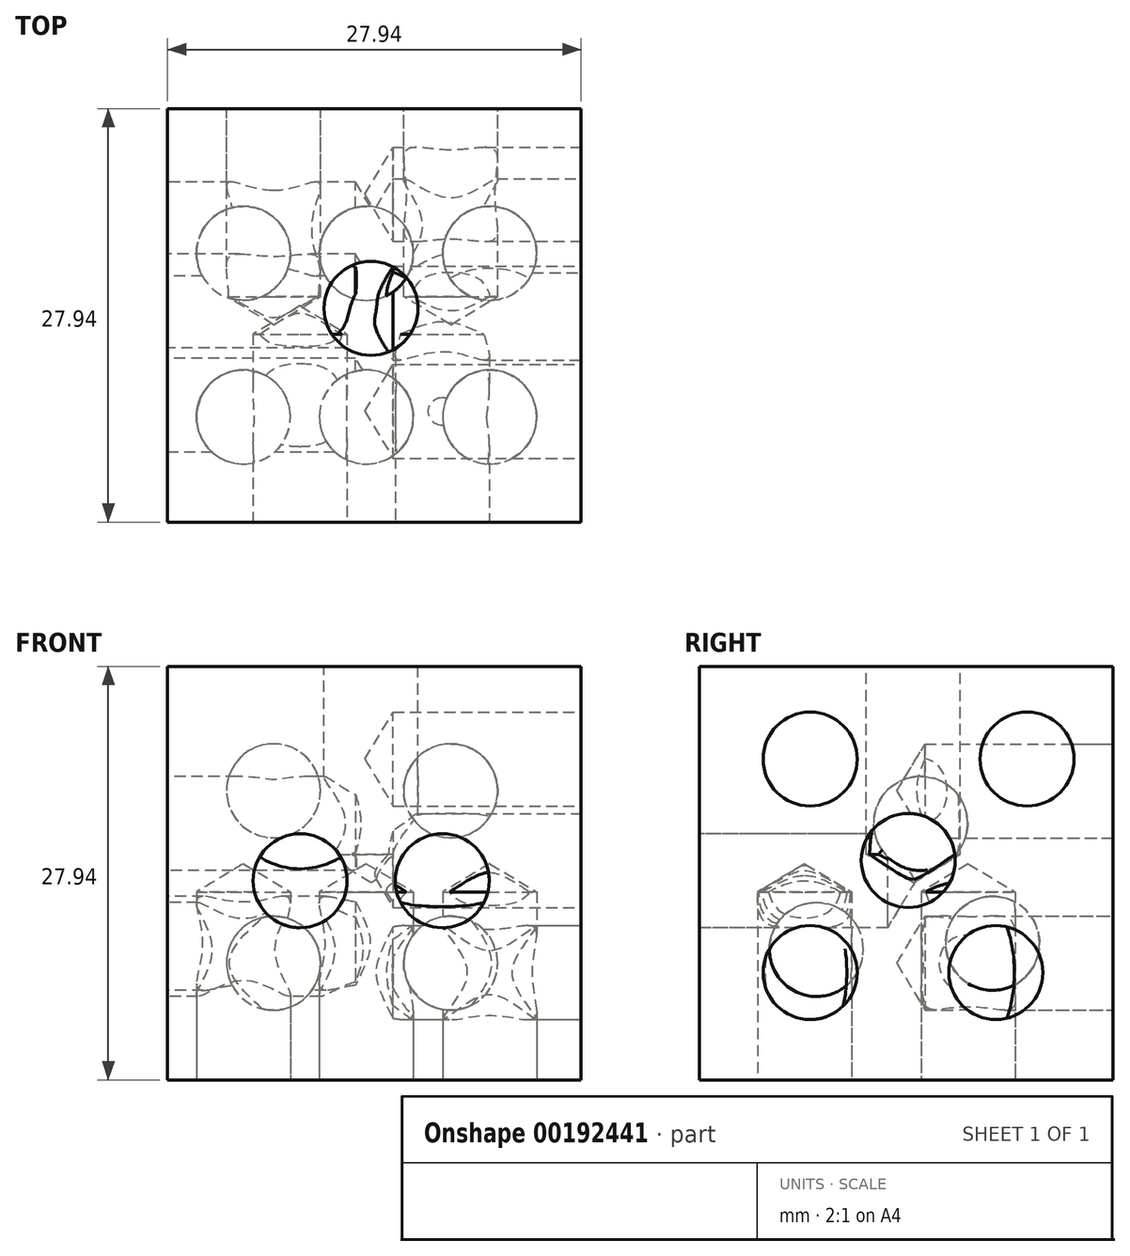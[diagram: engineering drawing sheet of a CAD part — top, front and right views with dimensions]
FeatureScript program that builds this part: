
annotation { "Feature Type Name" : "Feature", "Feature Type Description" : "" }
export const myFeature = defineFeature(function(context is Context, id is Id, definition is map)
    precondition{}
    {
        {
            var Q0;
            Q0=qCreatedBy(makeId("Top.planeOp"),FACE);
            var sketch = newSketch(context, id + "F0", { "sketchPlane" : qUnion([Q0])});
            skLineSegment(sketch, "E0.bottom", {"start": v(0, 0) * mm, "end": v(27.94, 0) * mm});
            skLineSegment(sketch, "E0.top", {"start": v(0, 27.94) * mm, "end": v(27.94, 27.94) * mm});
            skLineSegment(sketch, "E0.left", {"start": v(0, 0) * mm, "end": v(0, 27.94) * mm});
            skLineSegment(sketch, "E0.right", {"start": v(27.94, 0) * mm, "end": v(27.94, 27.94) * mm});
            skSolve(sketch);
        }
        {
            var Q0;
            Q0 = qSketchRegion(id + "F0", true);
            extrude(context, id + "F1", {"entities" : qUnion([Q0]), "depth" : 27.94 * mm});
        }
        {
            var Q0;
            Q0=makeQuery(id+"F1.opExtrude","CAP_FACE",FACE,{"disambiguationData":[OSD([sQuery(id+"F0.wireOp",EDGE,"E0.bottom"),sQuery(id+"F0.wireOp",EDGE,"E0.top"),sQuery(id+"F0.wireOp",EDGE,"E0.left"),sQuery(id+"F0.wireOp",EDGE,"E0.right")])],"isStart":false});
            var sketch = newSketch(context, id + "F2", { "sketchPlane" : qUnion([Q0])});
            skPoint(sketch, "E1", {"position": v(13.75, 14.44) * mm});
            skSolve(sketch);
        }
        {
            var Q0;
            Q0=makeQuery(id+"F1.opExtrude","SWEPT_FACE",FACE,{"disambiguationData":[OSD([sQuery(id+"F0.wireOp",EDGE,"E0.bottom")])]});
            var sketch = newSketch(context, id + "F3", { "sketchPlane" : qUnion([Q0])});
            skPoint(sketch, "E2", {"position": v(8.96, 13.45) * mm});
            skPoint(sketch, "E3", {"position": v(18.56, 13.45) * mm});
            skSolve(sketch);
        }
        {
            var Q0;
            Q0=makeQuery(id+"F1.opExtrude","SWEPT_FACE",FACE,{"disambiguationData":[OSD([sQuery(id+"F0.wireOp",EDGE,"E0.left")])]});
            var sketch = newSketch(context, id + "F4", { "sketchPlane" : qUnion([Q0])});
            skPoint(sketch, "E4", {"position": v(-7.9, 8.81) * mm});
            skPoint(sketch, "E5", {"position": v(-19.8, 9.22) * mm});
            skPoint(sketch, "E6", {"position": v(-14.94, 17.33) * mm});
            skSolve(sketch);
        }
        {
            var Q0;
            Q0=makeQuery(id+"F1.opExtrude","SWEPT_FACE",FACE,{"disambiguationData":[OSD([sQuery(id+"F0.wireOp",EDGE,"E0.top")])]});
            var sketch = newSketch(context, id + "F5", { "sketchPlane" : qUnion([Q0])});
            skPoint(sketch, "E7", {"position": v(-19.13, 19.53) * mm});
            skPoint(sketch, "E8", {"position": v(-7.16, 19.53) * mm});
            skPoint(sketch, "E9", {"position": v(-7.16, 7.88) * mm});
            skPoint(sketch, "E10", {"position": v(-19.13, 7.88) * mm});
            skSolve(sketch);
        }
        {
            var Q0;
            Q0=makeQuery(id+"F1.opExtrude","SWEPT_FACE",FACE,{"disambiguationData":[OSD([sQuery(id+"F0.wireOp",EDGE,"E0.right")])]});
            var sketch = newSketch(context, id + "F6", { "sketchPlane" : qUnion([Q0])});
            skPoint(sketch, "E11", {"position": v(7.47, 7.25) * mm});
            skPoint(sketch, "E12", {"position": v(7.47, 21.67) * mm});
            skPoint(sketch, "E13", {"position": v(22.13, 21.67) * mm});
            skPoint(sketch, "E14", {"position": v(20.02, 7.25) * mm});
            skPoint(sketch, "E15", {"position": v(14.1, 14.83) * mm});
            skSolve(sketch);
        }
        {
            var Q0;
            Q0=makeQuery(id+"F1.opExtrude","CAP_FACE",FACE,{"disambiguationData":[OSD([sQuery(id+"F0.wireOp",EDGE,"E0.bottom"),sQuery(id+"F0.wireOp",EDGE,"E0.top"),sQuery(id+"F0.wireOp",EDGE,"E0.left"),sQuery(id+"F0.wireOp",EDGE,"E0.right")])],"isStart":true});
            var sketch = newSketch(context, id + "F7", { "sketchPlane" : qUnion([Q0])});
            skPoint(sketch, "E16", {"position": v(21.77, -7.1) * mm});
            skPoint(sketch, "E17", {"position": v(13.43, -7.1) * mm});
            skPoint(sketch, "E18", {"position": v(5.13, -7.1) * mm});
            skPoint(sketch, "E19", {"position": v(5.13, -18.16) * mm});
            skPoint(sketch, "E20", {"position": v(13.43, -18.16) * mm});
            skPoint(sketch, "E21", {"position": v(21.77, -18.16) * mm});
            skSolve(sketch);
        }
        {
            var Q0;
            Q0=sQuery(id+"F2.wireOp",VERTEX,"E1");
            var Q1;
            Q1=sQuery(id+"F5.wireOp",VERTEX,"E8");
            var Q2;
            Q2=sQuery(id+"F5.wireOp",VERTEX,"E7");
            var Q3;
            Q3=sQuery(id+"F6.wireOp",VERTEX,"E13");
            var Q4;
            Q4=sQuery(id+"F6.wireOp",VERTEX,"E12");
            var Q5;
            Q5=sQuery(id+"F5.wireOp",VERTEX,"E10");
            var Q6;
            Q6=sQuery(id+"F6.wireOp",VERTEX,"E15");
            var Q7;
            Q7=sQuery(id+"F6.wireOp",VERTEX,"E14");
            var Q8;
            Q8=sQuery(id+"F7.wireOp",VERTEX,"E21");
            var Q9;
            Q9=sQuery(id+"F7.wireOp",VERTEX,"E16");
            var Q10;
            Q10=sQuery(id+"F7.wireOp",VERTEX,"E17");
            var Q11;
            Q11=sQuery(id+"F7.wireOp",VERTEX,"E20");
            var Q12;
            Q12=sQuery(id+"F3.wireOp",VERTEX,"E3");
            var Q13;
            Q13=sQuery(id+"F5.wireOp",VERTEX,"E9");
            var Q14;
            Q14=sQuery(id+"F4.wireOp",VERTEX,"E6");
            var Q15;
            Q15=sQuery(id+"F4.wireOp",VERTEX,"E5");
            var Q16;
            Q16=sQuery(id+"F3.wireOp",VERTEX,"E2");
            var Q17;
            Q17=sQuery(id+"F7.wireOp",VERTEX,"E19");
            var Q18;
            Q18=sQuery(id+"F7.wireOp",VERTEX,"E18");
            var Q19;
            Q19=sQuery(id+"F4.wireOp",VERTEX,"E4");
            var Q20;
            Q20=sQuery(id+"F6.wireOp",VERTEX,"E11");
            var Q21;
            Q21=makeQuery(id+"F1.opExtrude","SWEPT_BODY",BODY,{"disambiguationData":[OSD([sQuery(id+"F0.wireOp",EDGE,"E0.bottom"),sQuery(id+"F0.wireOp",EDGE,"E0.top"),sQuery(id+"F0.wireOp",EDGE,"E0.left"),sQuery(id+"F0.wireOp",EDGE,"E0.right")])]});
            hole(context, id + "F8", {"style" : HoleStyle.SIMPLE, "endStyle" : HoleEndStyle.BLIND, "holeDiameter" : 6.35 * mm, "holeDepth" : 12.7 * mm, "locations" : qUnion([Q0, Q1, Q2, Q3, Q4, Q5, Q6, Q7, Q8, Q9, Q10, Q11, Q12, Q13, Q14, Q15, Q16, Q17, Q18, Q19, Q20]), "scope" : qUnion([Q21])});
        }
    });
